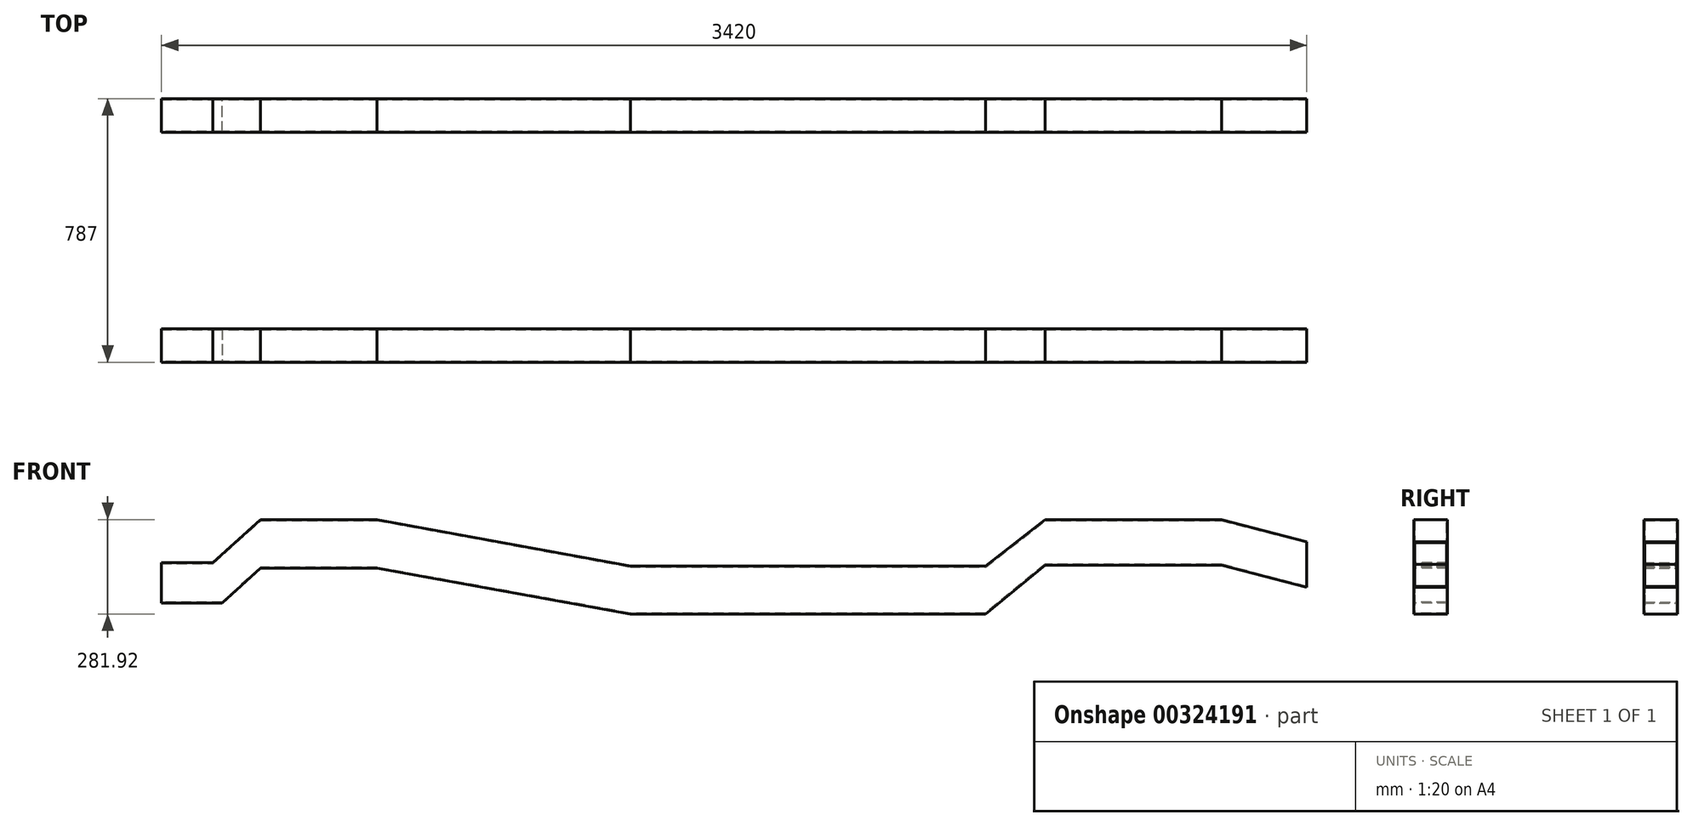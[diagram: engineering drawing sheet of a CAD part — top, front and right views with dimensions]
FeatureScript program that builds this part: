
annotation { "Feature Type Name" : "Feature", "Feature Type Description" : "" }
export const myFeature = defineFeature(function(context is Context, id is Id, definition is map)
    precondition{}
    {
        {
            var Q0;
            Q0=qCreatedBy(makeId("Front.planeOp"),FACE);
            cPlane(context, id + "F0", {"entities" : qUnion([Q0]), "cplaneType" : CPlaneType.OFFSET, "offset" : (787 / 2) * mm, "width" : 150 * mm, "height" : 150 * mm});
        }
        {
            var Q0;
            Q0=qCreatedBy(id+"F0.planeOp",FACE);
            var sketch = newSketch(context, id + "F1", { "sketchPlane" : qUnion([Q0])});
            skLineSegment(sketch, "E0", {"start": v(-1566.2, -129) * mm, "end": v(-1412.8, -129) * mm});
            skLineSegment(sketch, "E1", {"start": v(-1412.8, -129) * mm, "end": v(-1269.87, 0) * mm});
            skLineSegment(sketch, "E2", {"start": v(-1269.87, 0) * mm, "end": v(-922.45, 0) * mm});
            skLineSegment(sketch, "E3", {"start": v(-922.45, 0) * mm, "end": v(-165.94, -138.85) * mm});
            skLineSegment(sketch, "E4", {"start": v(-165.94, -138.85) * mm, "end": v(895.08, -138.85) * mm});
            skLineSegment(sketch, "E5", {"start": v(895.08, -138.85) * mm, "end": v(1072.88, 0) * mm});
            skLineSegment(sketch, "E6", {"start": v(1072.88, 0) * mm, "end": v(1599.3, 0) * mm});
            skLineSegment(sketch, "E7", {"start": v(1599.3, 0) * mm, "end": v(1853.8, -66.24) * mm});
            skLineSegment(sketch, "E8", {"start": v(1853.8, -66.24) * mm, "end": v(1853.8, -202.2) * mm});
            skLineSegment(sketch, "E9", {"start": v(1853.8, -202.2) * mm, "end": v(1599.3, -135.96) * mm});
            skLineSegment(sketch, "E10", {"start": v(1599.3, -135.96) * mm, "end": v(1072.88, -135.96) * mm});
            skLineSegment(sketch, "E11", {"start": v(1072.88, -135.96) * mm, "end": v(895.08, -281.92) * mm});
            skLineSegment(sketch, "E12", {"start": v(895.08, -281.92) * mm, "end": v(-165.94, -281.92) * mm});
            skLineSegment(sketch, "E13", {"start": v(-165.94, -281.92) * mm, "end": v(-922.45, -145.43) * mm});
            skLineSegment(sketch, "E14", {"start": v(-922.45, -145.43) * mm, "end": v(-1269.87, -145.43) * mm});
            skLineSegment(sketch, "E15", {"start": v(-1269.87, -145.43) * mm, "end": v(-1384.33, -248.72) * mm});
            skLineSegment(sketch, "E16", {"start": v(-1384.33, -248.72) * mm, "end": v(-1566.2, -248.72) * mm});
            skLineSegment(sketch, "E17", {"start": v(-1566.2, -248.72) * mm, "end": v(-1566.2, -129) * mm});
            skLineSegment(sketch, "E18", {"start": v(-922.45, 0) * mm, "end": v(1072.88, 0) * mm, "construction": true});
            skSolve(sketch);
        }
        {
            var Q0;
            Q0=makeQuery(id+"F1.imprint","IMPRINT",FACE,{"disambiguationData":[TD([[makeQuery(id+"F1.imprint","IMPRINT",EDGE,{"derivedFrom":sQuery(id+"F1.wireOp",EDGE,"E0")}),-1.0]])]});
            extrude(context, id + "F2", {"entities" : qUnion([Q0]), "oppositeDirection" : true, "depth" : 100 * mm, "offsetDistance" : 25 * mm});
        }
        {
            var Q0;
            Q0=makeQuery(id+"F2.opExtrude","SWEPT_FACE",FACE,{"disambiguationData":[OSD([sQuery(id+"F1.wireOp",EDGE,"E17")])]});
            var Q1;
            Q1=makeQuery(id+"F2.opExtrude","SWEPT_FACE",FACE,{"disambiguationData":[OSD([sQuery(id+"F1.wireOp",EDGE,"E8")])]});
            shell(context, id + "F3", {"entities" : qUnion([Q0, Q1]), "thickness" : 2.5 * mm});
        }
        {
            var Q0;
            Q0=makeQuery(id+"F2.opExtrude","SWEPT_BODY",BODY,{"disambiguationData":[OSD([sQuery(id+"F1.wireOp",EDGE,"E0"),sQuery(id+"F1.wireOp",EDGE,"E1"),sQuery(id+"F1.wireOp",EDGE,"E2"),sQuery(id+"F1.wireOp",EDGE,"E3"),sQuery(id+"F1.wireOp",EDGE,"E4"),sQuery(id+"F1.wireOp",EDGE,"E5"),sQuery(id+"F1.wireOp",EDGE,"E6"),sQuery(id+"F1.wireOp",EDGE,"E7"),sQuery(id+"F1.wireOp",EDGE,"E8"),sQuery(id+"F1.wireOp",EDGE,"E9"),sQuery(id+"F1.wireOp",EDGE,"E10"),sQuery(id+"F1.wireOp",EDGE,"E11"),sQuery(id+"F1.wireOp",EDGE,"E12"),sQuery(id+"F1.wireOp",EDGE,"E13"),sQuery(id+"F1.wireOp",EDGE,"E14"),sQuery(id+"F1.wireOp",EDGE,"E15"),sQuery(id+"F1.wireOp",EDGE,"E16"),sQuery(id+"F1.wireOp",EDGE,"E17")])]});
            var Q1;
            Q1=qCreatedBy(makeId("Front.planeOp"),FACE);
            mirror(context, id + "F4", {"entities" : qUnion([Q0]), "mirrorPlane" : qUnion([Q1])});
        }
    });
